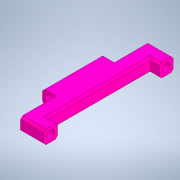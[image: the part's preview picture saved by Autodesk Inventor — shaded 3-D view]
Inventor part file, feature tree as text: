
AUTODESK INVENTOR PART (.ipt)
format: ipt  version: 2020 (Build 240168000, 168)  size: 157,696 bytes
history: native  units: mm
features: extrude x3, sketch x3, chamfer x1
ambient origin geometry x8: Origin, YZ Plane, XZ Plane, XY Plane, X Axis, Y Axis, Z Axis, Center Point
bodies: Solid1 (feature_tree)
feature tree (7):
  extrude  "Extrusion1"  Depth=6.0mm
  extrude  "Extrusion2"  Depth=6.0mm
  extrude  "Extrusion3"  Depth=6.0mm TaperAngle=0.0deg
  chamfer  "Chamfer1"  Distance=3.4mm
  sketch  "Sketch1"  dims[d0=25.0mm d1=6.0mm]
  sketch  "Sketch2"  dims[d2=50.0mm d3=6.0mm]
  sketch  "Sketch3"  dims[d4=4.0mm d6=6.0mm d7=0.0mm d8=3.4mm d9=0.0mm d10=0.0mm d11=3.4mm d12=0.0mm d13=0.0mm d14=1.0mm d15=2.0mm d16=45.0deg d17=6.0mm]
